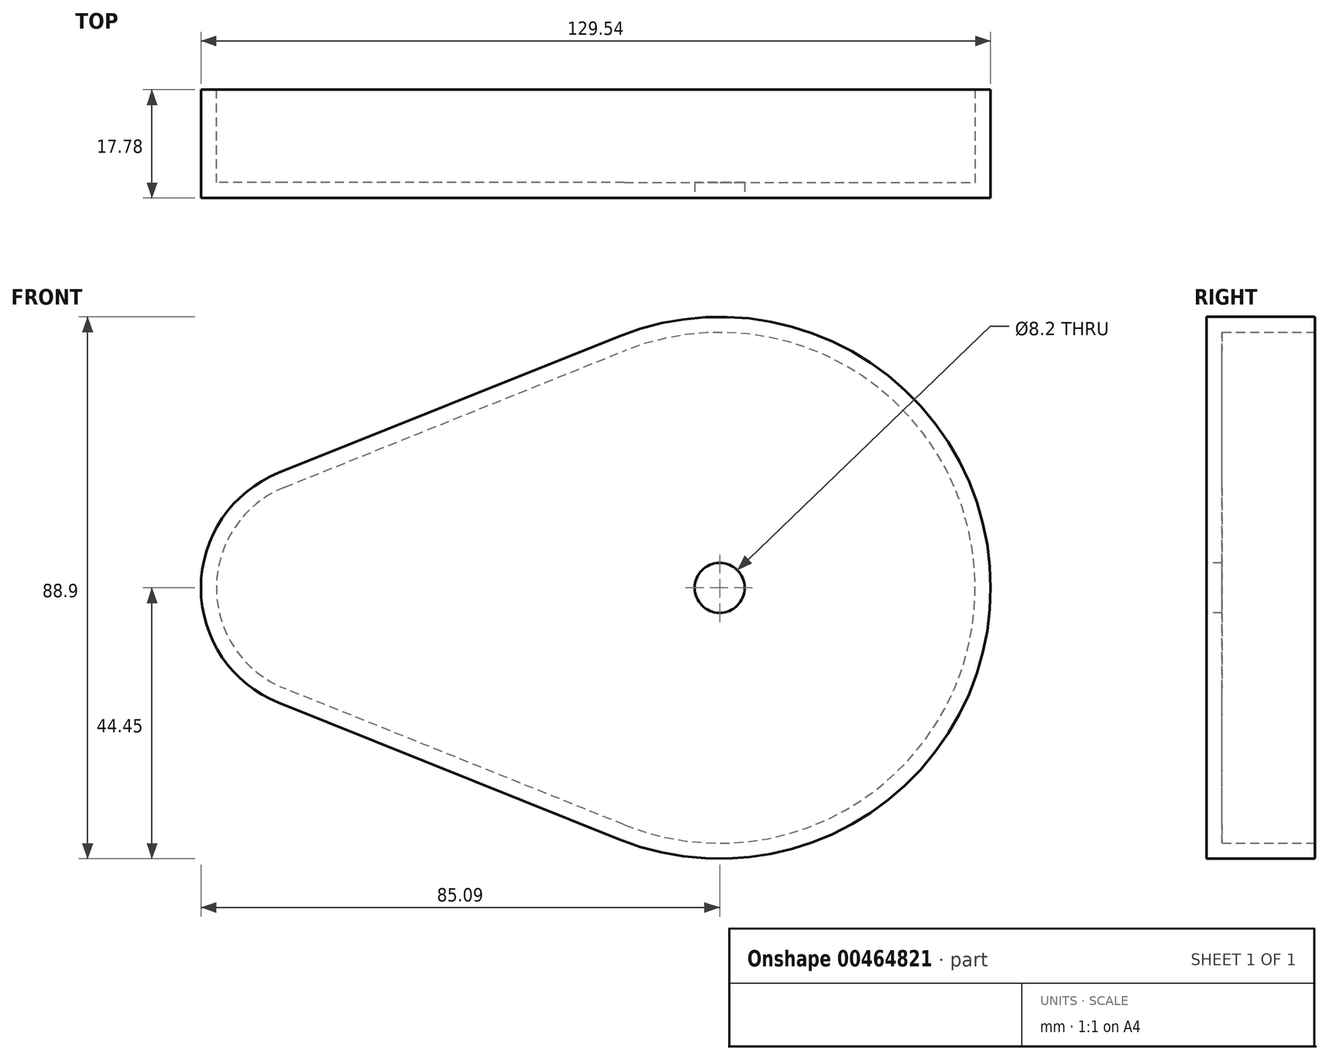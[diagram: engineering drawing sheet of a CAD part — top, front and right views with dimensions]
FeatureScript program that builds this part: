
annotation { "Feature Type Name" : "Feature", "Feature Type Description" : "" }
export const myFeature = defineFeature(function(context is Context, id is Id, definition is map)
    precondition{}
    {
        {
            var Q0;
            Q0=qCreatedBy(makeId("Front.planeOp"),FACE);
            var sketch = newSketch(context, id + "F0", { "sketchPlane" : qUnion([Q0])});
            skArc(sketch, "E0", {"start": v(-7.57, 18.86) * mm, "mid": v(-20.32, 0) * mm, "end": v(-7.57, -18.86) * mm});
            skArc(sketch, "E1", {"start": v(48.21, -41.25) * mm, "mid": v(109.22, 0) * mm, "end": v(48.21, 41.25) * mm});
            skLineSegment(sketch, "E2", {"start": v(48.21, -41.25) * mm, "end": v(-7.57, -18.86) * mm});
            skLineSegment(sketch, "E3", {"start": v(-7.57, -18.86) * mm, "end": v(-7.57, 18.86) * mm, "construction": true});
            skLineSegment(sketch, "E4", {"start": v(-7.57, 18.86) * mm, "end": v(48.21, 41.25) * mm});
            skLineSegment(sketch, "E5", {"start": v(48.21, 41.25) * mm, "end": v(48.21, -41.25) * mm, "construction": true});
            skSolve(sketch);
        }
        {
            var Q0;
            Q0 = qSketchRegion(id + "F0", true);
            extrude(context, id + "F1", {"entities" : qUnion([Q0]), "depth" : 17.78 * mm, "offsetDistance" : 25.4 * mm});
        }
        {
            var Q0;
            Q0=makeQuery(id+"F1.opExtrude","CAP_FACE",FACE,{"disambiguationData":[OSD([sQuery(id+"F0.wireOp",EDGE,"E0"),sQuery(id+"F0.wireOp",EDGE,"E1"),sQuery(id+"F0.wireOp",EDGE,"E2"),sQuery(id+"F0.wireOp",EDGE,"E4")])],"isStart":true});
            shell(context, id + "F2", {"entities" : qUnion([Q0]), "thickness" : 2.54 * mm});
        }
        {
            var Q0;
            Q0=makeQuery(id+"F1.opExtrude","CAP_FACE",FACE,{"disambiguationData":[OSD([sQuery(id+"F0.wireOp",EDGE,"E0"),sQuery(id+"F0.wireOp",EDGE,"E1"),sQuery(id+"F0.wireOp",EDGE,"E2"),sQuery(id+"F0.wireOp",EDGE,"E4")])],"isStart":false});
            var sketch = newSketch(context, id + "F3", { "sketchPlane" : qUnion([Q0])});
            skCircle(sketch, "E6", {"center": v(64.77, 0) * mm, "radius": 4.1 * mm});
            skSolve(sketch);
        }
        {
            var Q0;
            Q0 = qSketchRegion(id + "F3", true);
            extrude(context, id + "F4", {"entities" : qUnion([Q0]), "operationType" : NewBodyOperationType.REMOVE, "oppositeDirection" : true, "depth" : 25.4 * mm, "offsetDistance" : 25.4 * mm});
        }
    });
